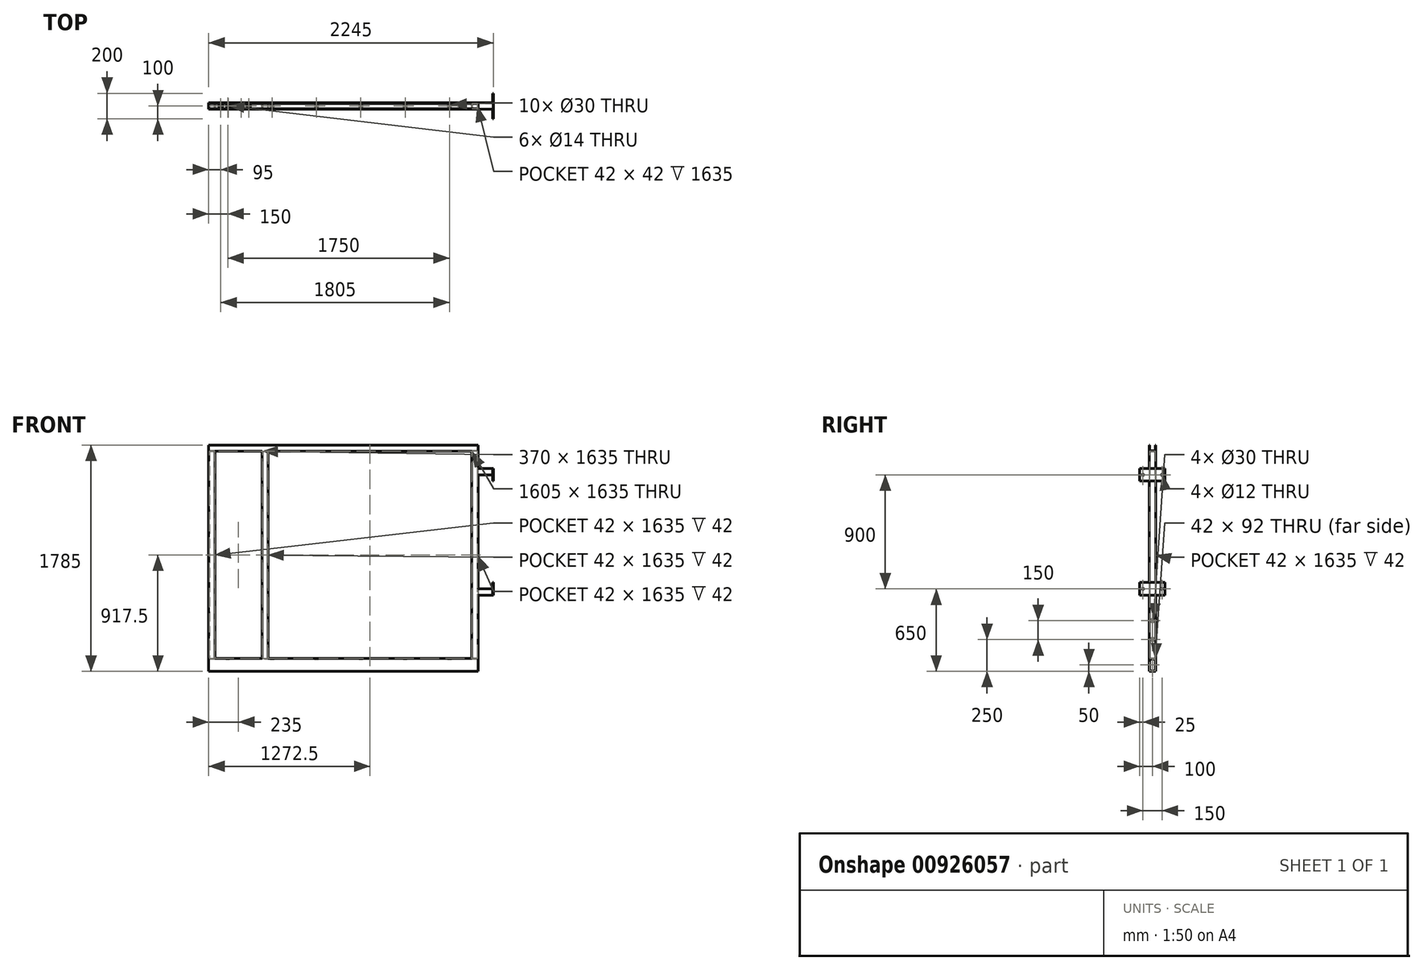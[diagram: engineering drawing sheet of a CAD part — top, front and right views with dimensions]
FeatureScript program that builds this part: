
annotation { "Feature Type Name" : "Feature", "Feature Type Description" : "" }
export const myFeature = defineFeature(function(context is Context, id is Id, definition is map)
    precondition{}
    {
        {
            var Q0;
            Q0=qCreatedBy(makeId("Top.planeOp"),FACE);
            var sketch = newSketch(context, id + "F0", { "sketchPlane" : qUnion([Q0])});
            skLineSegment(sketch, "E0.bottom", {"start": v(0, 0) * mm, "end": v(50, 0) * mm});
            skLineSegment(sketch, "E0.top", {"start": v(0, 50) * mm, "end": v(50, 50) * mm});
            skLineSegment(sketch, "E0.left", {"start": v(0, 0) * mm, "end": v(0, 4) * mm});
            skLineSegment(sketch, "E0.right", {"start": v(50, 0) * mm, "end": v(50, 50) * mm});
            skLineSegment(sketch, "E1.bottom", {"start": v(4, 46) * mm, "end": v(46, 46) * mm});
            skLineSegment(sketch, "E1.top", {"start": v(4, 4) * mm, "end": v(46, 4) * mm});
            skLineSegment(sketch, "E1.right", {"start": v(46, 46) * mm, "end": v(46, 4) * mm});
            skLineSegment(sketch, "E2", {"start": v(12.25, 50) * mm, "end": v(12.25, 46) * mm, "construction": true});
            skPoint(sketch, "E2.endSnap0", {"position": v(23, 46) * mm});
            skLineSegment(sketch, "E3", {"start": v(46, 38.8) * mm, "end": v(50, 38.8) * mm, "construction": true});
            skLineSegment(sketch, "E4", {"start": v(20.28, 4) * mm, "end": v(20.28, 0) * mm, "construction": true});
            skLineSegment(sketch, "E5.trimOffspring", {"start": v(0, 46) * mm, "end": v(0, 50) * mm});
            skLineSegment(sketch, "E6", {"start": v(0, 46) * mm, "end": v(0, 4) * mm});
            skLineSegment(sketch, "E7", {"start": v(4, 46) * mm, "end": v(4, 4) * mm});
            skSolve(sketch);
        }
        {
            var Q0;
            Q0 = qSketchRegion(id + "F0", true);
            extrude(context, id + "F1", {"entities" : qUnion([Q0]), "depth" : (1800 - 15 - 100 - 50) * mm, "offsetDistance" : 25 * mm});
        }
        {
            var Q0;
            Q0=makeQuery(id+"F1.opExtrude","SWEPT_FACE",FACE,{"disambiguationData":[OSD([sQuery(id+"F0.wireOp",EDGE,"E5.trimOffspring")])]});
            var sketch = newSketch(context, id + "F2", { "sketchPlane" : qUnion([Q0])});
            skLineSegment(sketch, "E8.bottom", {"start": v(-50, 0) * mm, "end": v(0, 0) * mm});
            skLineSegment(sketch, "E8.top", {"start": v(-50, -100) * mm, "end": v(0, -100) * mm});
            skLineSegment(sketch, "E8.left", {"start": v(-50, 0) * mm, "end": v(-50, -100) * mm});
            skLineSegment(sketch, "E8.right", {"start": v(0, 0) * mm, "end": v(0, -100) * mm});
            skLineSegment(sketch, "E9.bottom", {"start": v(-46, -4) * mm, "end": v(-4, -4) * mm});
            skLineSegment(sketch, "E9.top", {"start": v(-46, -96) * mm, "end": v(-4, -96) * mm});
            skLineSegment(sketch, "E9.left", {"start": v(-50, -4) * mm, "end": v(-50, -96) * mm});
            skLineSegment(sketch, "E9.right", {"start": v(-4, -4) * mm, "end": v(-4, -96) * mm});
            skLineSegment(sketch, "E10", {"start": v(-25, 0) * mm, "end": v(-25, -4) * mm, "construction": true});
            skLineSegment(sketch, "E11", {"start": v(-50, -50) * mm, "end": v(-50, -50) * mm});
            skLineSegment(sketch, "E12", {"start": v(-25, -100) * mm, "end": v(-25, -96) * mm, "construction": true});
            skLineSegment(sketch, "E13", {"start": v(-4, -50) * mm, "end": v(0, -50) * mm, "construction": true});
            skLineSegment(sketch, "E14", {"start": v(-46, -4) * mm, "end": v(-46, -96) * mm});
            skLineSegment(sketch, "E15", {"start": v(-46, -50) * mm, "end": v(-50, -50) * mm, "construction": true});
            skSolve(sketch);
        }
        {
            var Q0;
            Q0=makeQuery(id+"F2.imprint","IMPRINT",FACE,{"disambiguationData":[TD([[makeQuery(id+"F2.imprint","IMPRINT",EDGE,{"derivedFrom":sQuery(id+"F2.wireOp",EDGE,"E8.top")}),1.0]])]});
            extrude(context, id + "F3", {"entities" : qUnion([Q0]), "oppositeDirection" : true, "depth" : (100 + 1540 + 500 - 15) * mm, "offsetDistance" : 25 * mm});
        }
        {
            var Q0;
            Q0=qCreatedBy(makeId("Right.planeOp"),FACE);
            cPlane(context, id + "F4", {"entities" : qUnion([Q0]), "cplaneType" : CPlaneType.OFFSET, "offset" : (2125 / 2) * mm, "width" : 150 * mm, "height" : 150 * mm});
        }
        {
            var Q0;
            Q0=makeQuery(id+"F1.opExtrude","SWEPT_BODY",BODY,{"disambiguationData":[OSD([sQuery(id+"F0.wireOp",EDGE,"E0.bottom"),sQuery(id+"F0.wireOp",EDGE,"E0.top"),sQuery(id+"F0.wireOp",EDGE,"E0.left"),sQuery(id+"F0.wireOp",EDGE,"E0.right"),sQuery(id+"F0.wireOp",EDGE,"E1.bottom"),sQuery(id+"F0.wireOp",EDGE,"E1.top"),sQuery(id+"F0.wireOp",EDGE,"E1.right"),sQuery(id+"F0.wireOp",EDGE,"E5.trimOffspring")])]});
            var Q1;
            Q1=qCreatedBy(id+"F4.planeOp",FACE);
            mirror(context, id + "F5", {"operationType" : NewBodyOperationType.ADD, "entities" : qUnion([Q0]), "mirrorPlane" : qUnion([Q1])});
        }
        {
            var Q0;
            Q0=makeQuery(id+"F5.boolean.opBoolean","MERGE",FACE,{"derivedFrom":[makeQuery(id+"F1.opExtrude","SWEPT_FACE",FACE,{"disambiguationData":[OSD([sQuery(id+"F0.wireOp",EDGE,"E0.left")])]}),makeQuery(id+"F1.opExtrude","SWEPT_FACE",FACE,{"disambiguationData":[OSD([sQuery(id+"F0.wireOp",EDGE,"E5.trimOffspring")])]}),makeQuery(id+"F3.opExtrude","CAP_FACE",FACE,{"disambiguationData":[OSD([sQuery(id+"F2.wireOp",EDGE,"E8.bottom"),sQuery(id+"F2.wireOp",EDGE,"E8.top"),sQuery(id+"F2.wireOp",EDGE,"E8.left"),sQuery(id+"F2.wireOp",EDGE,"E8.right"),sQuery(id+"F2.wireOp",EDGE,"E9.bottom"),sQuery(id+"F2.wireOp",EDGE,"E9.top"),sQuery(id+"F2.wireOp",EDGE,"E9.left"),sQuery(id+"F2.wireOp",EDGE,"E9.right")])],"isStart":true})]});
            var sketch = newSketch(context, id + "F6", { "sketchPlane" : qUnion([Q0])});
            skLineSegment(sketch, "E16.bottom", {"start": v(-50, 1685) * mm, "end": v(-46, 1685) * mm});
            skLineSegment(sketch, "E16.top", {"start": v(-50, 1635) * mm, "end": v(0, 1635) * mm});
            skLineSegment(sketch, "E16.left", {"start": v(-50, 1685) * mm, "end": v(-50, 1635) * mm});
            skLineSegment(sketch, "E16.right", {"start": v(0, 1685) * mm, "end": v(0, 1635) * mm});
            skLineSegment(sketch, "E17.top", {"start": v(-46, 1639) * mm, "end": v(-4, 1639) * mm});
            skLineSegment(sketch, "E17.left", {"start": v(-46, 1685) * mm, "end": v(-46, 1639) * mm});
            skLineSegment(sketch, "E17.right", {"start": v(-4, 1685) * mm, "end": v(-4, 1639) * mm});
            skLineSegment(sketch, "E18", {"start": v(-25, 1639) * mm, "end": v(-25, 1635) * mm, "construction": true});
            skLineSegment(sketch, "E19.trimOffspring", {"start": v(-4, 1685) * mm, "end": v(0, 1685) * mm});
            skSolve(sketch);
        }
        {
            var Q0;
            Q0 = qSketchRegion(id + "F6", true);
            var Q1;
            Q1=makeQuery(id+"F5.boolean.opBoolean","MERGE",FACE,{"derivedFrom":[makeQuery(id+"F3.opExtrude","CAP_FACE",FACE,{"disambiguationData":[OSD([sQuery(id+"F2.wireOp",EDGE,"E8.bottom"),sQuery(id+"F2.wireOp",EDGE,"E8.top"),sQuery(id+"F2.wireOp",EDGE,"E8.left"),sQuery(id+"F2.wireOp",EDGE,"E8.right"),sQuery(id+"F2.wireOp",EDGE,"E9.bottom"),sQuery(id+"F2.wireOp",EDGE,"E9.top"),sQuery(id+"F2.wireOp",EDGE,"E9.left"),sQuery(id+"F2.wireOp",EDGE,"E9.right")])],"isStart":false}),makeQuery(id+"F5.opPattern","COPY",FACE,{"derivedFrom":makeQuery(id+"F1.opExtrude","SWEPT_FACE",FACE,{"disambiguationData":[OSD([sQuery(id+"F0.wireOp",EDGE,"E0.left")])]}),"instanceName":"1"}),makeQuery(id+"F5.opPattern","COPY",FACE,{"derivedFrom":makeQuery(id+"F1.opExtrude","SWEPT_FACE",FACE,{"disambiguationData":[OSD([sQuery(id+"F0.wireOp",EDGE,"E5.trimOffspring")])]}),"instanceName":"1"})]});
            extrude(context, id + "F7", {"entities" : qUnion([Q0]), "operationType" : NewBodyOperationType.ADD, "endBound" : BoundingType.UP_TO_SURFACE, "oppositeDirection" : true, "depth" : 25 * mm, "endBoundEntityFace" : qUnion([Q1]), "offsetDistance" : 25 * mm});
        }
        {
            var Q0;
            Q0=makeQuery(id+"F7.opExtrude","SWEPT_FACE",FACE,{"disambiguationData":[OSD([sQuery(id+"F6.wireOp",EDGE,"E17.top")])]});
            var sketch = newSketch(context, id + "F8", { "sketchPlane" : qUnion([Q0])});
            skLineSegment(sketch, "E20", {"start": v(2125, 25) * mm, "end": v(365, 25) * mm, "construction": true});
            skLineSegment(sketch, "E21", {"start": v(365, 4) * mm, "end": v(365, 46) * mm, "construction": true});
            skCircle(sketch, "E22", {"center": v(315, 25) * mm, "radius": 15 * mm});
            skCircle(sketch, "E23", {"center": v(155, 25) * mm, "radius": 15 * mm});
            skCircle(sketch, "E24", {"center": v(255, 25) * mm, "radius": 15 * mm});
            skCircle(sketch, "E25", {"center": v(95, 25) * mm, "radius": 15 * mm});
            skLineSegment(sketch, "E26", {"start": v(365, 25) * mm, "end": v(45, 25) * mm, "construction": true});
            skLineSegment(sketch, "E27", {"start": v(45, -20.75) * mm, "end": v(45, 62.6) * mm, "construction": true});
            skSolve(sketch);
        }
        {
            var Q0;
            Q0 = qSketchRegion(id + "F8", true);
            extrude(context, id + "F9", {"entities" : qUnion([Q0]), "operationType" : NewBodyOperationType.REMOVE, "oppositeDirection" : true, "depth" : 50 * mm, "offsetDistance" : 25 * mm});
        }
        {
            var Q0;
            Q0=makeQuery(id+"F1.opExtrude","SWEPT_FACE",FACE,{"disambiguationData":[OSD([sQuery(id+"F0.wireOp",EDGE,"E0.right")])]});
            var sketch = newSketch(context, id + "F10", { "sketchPlane" : qUnion([Q0])});
            skCircle(sketch, "E28", {"center": v(25, 300) * mm, "radius": 15 * mm});
            skLineSegment(sketch, "E29", {"start": v(25, 0) * mm, "end": v(25, 300) * mm, "construction": true});
            skCircle(sketch, "E30", {"center": v(25, 150) * mm, "radius": 15 * mm});
            skSolve(sketch);
        }
        {
            var Q0;
            Q0 = qSketchRegion(id + "F10", true);
            extrude(context, id + "F11", {"entities" : qUnion([Q0]), "operationType" : NewBodyOperationType.REMOVE, "oppositeDirection" : true, "depth" : 250 * mm, "offsetDistance" : 25 * mm});
        }
        {
            var Q0;
            Q0=makeQuery(id+"F7.boolean.opBoolean","MERGE",FACE,{"derivedFrom":[makeQuery(id+"F5.boolean.opBoolean","MERGE",FACE,{"derivedFrom":[makeQuery(id+"F3.opExtrude","CAP_FACE",FACE,{"disambiguationData":[OSD([sQuery(id+"F2.wireOp",EDGE,"E8.bottom"),sQuery(id+"F2.wireOp",EDGE,"E8.top"),sQuery(id+"F2.wireOp",EDGE,"E8.left"),sQuery(id+"F2.wireOp",EDGE,"E8.right"),sQuery(id+"F2.wireOp",EDGE,"E9.bottom"),sQuery(id+"F2.wireOp",EDGE,"E9.top"),sQuery(id+"F2.wireOp",EDGE,"E9.left"),sQuery(id+"F2.wireOp",EDGE,"E9.right")])],"isStart":false}),makeQuery(id+"F5.opPattern","COPY",FACE,{"derivedFrom":makeQuery(id+"F1.opExtrude","SWEPT_FACE",FACE,{"disambiguationData":[OSD([sQuery(id+"F0.wireOp",EDGE,"E0.left")])]}),"instanceName":"1"}),makeQuery(id+"F5.opPattern","COPY",FACE,{"derivedFrom":makeQuery(id+"F1.opExtrude","SWEPT_FACE",FACE,{"disambiguationData":[OSD([sQuery(id+"F0.wireOp",EDGE,"E5.trimOffspring")])]}),"instanceName":"1"})]}),makeQuery(id+"F7.opExtrude","CAP_FACE",FACE,{"disambiguationData":[OSD([sQuery(id+"F6.wireOp",EDGE,"E16.bottom"),sQuery(id+"F6.wireOp",EDGE,"E16.top"),sQuery(id+"F6.wireOp",EDGE,"E16.left"),sQuery(id+"F6.wireOp",EDGE,"E16.right"),sQuery(id+"F6.wireOp",EDGE,"E17.top"),sQuery(id+"F6.wireOp",EDGE,"E17.left"),sQuery(id+"F6.wireOp",EDGE,"E17.right"),sQuery(id+"F6.wireOp",EDGE,"E19.trimOffspring")])],"isStart":false})]});
            var sketch = newSketch(context, id + "F12", { "sketchPlane" : qUnion([Q0])});
            skLineSegment(sketch, "E31.bottom", {"start": v(0, 550) * mm, "end": v(4, 550) * mm});
            skLineSegment(sketch, "E31.top", {"start": v(0, 500) * mm, "end": v(50, 500) * mm});
            skLineSegment(sketch, "E31.left", {"start": v(0, 550) * mm, "end": v(0, 500) * mm});
            skLineSegment(sketch, "E31.right", {"start": v(50, 550) * mm, "end": v(50, 500) * mm});
            skLineSegment(sketch, "E32.top", {"start": v(4, 504) * mm, "end": v(46, 504) * mm});
            skLineSegment(sketch, "E32.left", {"start": v(4, 550) * mm, "end": v(4, 504) * mm});
            skLineSegment(sketch, "E32.right", {"start": v(46, 550) * mm, "end": v(46, 504) * mm});
            skLineSegment(sketch, "E33.trimOffspring", {"start": v(46, 550) * mm, "end": v(50, 550) * mm});
            skLineSegment(sketch, "E34", {"start": v(-400.98, 1000) * mm, "end": v(496.26, 1000) * mm, "construction": true});
            skLineSegment(sketch, "E35.MirrorCS", {"start": v(0, 1450) * mm, "end": v(4, 1450) * mm});
            skLineSegment(sketch, "E36.MirrorCS", {"start": v(46, 1450) * mm, "end": v(50, 1450) * mm});
            skLineSegment(sketch, "E37.MirrorCS", {"start": v(46, 1450) * mm, "end": v(46, 1496) * mm});
            skLineSegment(sketch, "E38.MirrorCS", {"start": v(50, 1450) * mm, "end": v(50, 1500) * mm});
            skLineSegment(sketch, "E39.MirrorCS", {"start": v(0, 1450) * mm, "end": v(0, 1500) * mm});
            skLineSegment(sketch, "E40.MirrorCS", {"start": v(4, 1496) * mm, "end": v(46, 1496) * mm});
            skLineSegment(sketch, "E41.MirrorCS", {"start": v(4, 1450) * mm, "end": v(4, 1496) * mm});
            skLineSegment(sketch, "E42.MirrorCS", {"start": v(0, 1500) * mm, "end": v(50, 1500) * mm});
            skSolve(sketch);
        }
        {
            var Q0;
            Q0 = qSketchRegion(id + "F12", true);
            extrude(context, id + "F13", {"entities" : qUnion([Q0]), "operationType" : NewBodyOperationType.ADD, "depth" : 116 * mm, "offsetDistance" : 25 * mm});
        }
        {
            var Q0;
            Q0=makeQuery(id+"F13.opExtrude","CAP_FACE",FACE,{"disambiguationData":[OSD([sQuery(id+"F12.wireOp",EDGE,"E35.MirrorCS"),sQuery(id+"F12.wireOp",EDGE,"E36.MirrorCS"),sQuery(id+"F12.wireOp",EDGE,"E37.MirrorCS"),sQuery(id+"F12.wireOp",EDGE,"E38.MirrorCS"),sQuery(id+"F12.wireOp",EDGE,"E39.MirrorCS"),sQuery(id+"F12.wireOp",EDGE,"E40.MirrorCS"),sQuery(id+"F12.wireOp",EDGE,"E41.MirrorCS"),sQuery(id+"F12.wireOp",EDGE,"E42.MirrorCS")])],"isStart":false});
            var sketch = newSketch(context, id + "F14", { "sketchPlane" : qUnion([Q0])});
            skLineSegment(sketch, "E43.bottom", {"start": v(125, 1500) * mm, "end": v(-75, 1500) * mm});
            skLineSegment(sketch, "E43.top", {"start": v(125, 1400) * mm, "end": v(-75, 1400) * mm});
            skLineSegment(sketch, "E43.left", {"start": v(125, 1500) * mm, "end": v(125, 1400) * mm});
            skLineSegment(sketch, "E43.right", {"start": v(-75, 1500) * mm, "end": v(-75, 1400) * mm});
            skPoint(sketch, "E44", {"position": v(25, 1500) * mm});
            skLineSegment(sketch, "E45.bottom", {"start": v(125, 600) * mm, "end": v(-75, 600) * mm});
            skLineSegment(sketch, "E45.top", {"start": v(125, 500) * mm, "end": v(-75, 500) * mm});
            skLineSegment(sketch, "E45.left", {"start": v(125, 600) * mm, "end": v(125, 500) * mm});
            skLineSegment(sketch, "E45.right", {"start": v(-75, 600) * mm, "end": v(-75, 500) * mm});
            skPoint(sketch, "E46", {"position": v(25, 500) * mm});
            skCircle(sketch, "E47", {"center": v(100, 1450) * mm, "radius": 6 * mm});
            skLineSegment(sketch, "E48", {"start": v(-50, 1450) * mm, "end": v(100, 1450) * mm, "construction": true});
            skLineSegment(sketch, "E49", {"start": v(25, 1400) * mm, "end": v(25, 1450) * mm, "construction": true});
            skLineSegment(sketch, "E50", {"start": v(-50, 550) * mm, "end": v(100, 550) * mm, "construction": true});
            skPoint(sketch, "E50.startSnap0", {"position": v(-75, 550) * mm});
            skLineSegment(sketch, "E51", {"start": v(25, 550) * mm, "end": v(25, 500) * mm, "construction": true});
            skCircle(sketch, "E52", {"center": v(-50, 550) * mm, "radius": 6 * mm});
            skCircle(sketch, "E53", {"center": v(100, 550) * mm, "radius": 6 * mm});
            skCircle(sketch, "E54", {"center": v(-50, 1450) * mm, "radius": 6 * mm});
            skSolve(sketch);
        }
        {
            var Q0;
            Q0 = qSketchRegion(id + "F14", true);
            extrude(context, id + "F15", {"entities" : qUnion([Q0]), "operationType" : NewBodyOperationType.ADD, "depth" : 4 * mm, "offsetDistance" : 25 * mm});
        }
        {
            var Q0;
            {var subQ2=makeQuery(id+"F1.opExtrude","SWEPT_FACE",FACE,{"disambiguationData":[OSD([sQuery(id+"F0.wireOp",EDGE,"E0.bottom")])]});Q0=makeQuery(id+"F5.boolean.opBoolean","SPLIT",FACE,{"disambiguationData":[TD([subQ2])],"derivedFrom":makeQuery(id+"F3.opExtrude","SWEPT_FACE",FACE,{"disambiguationData":[OSD([sQuery(id+"F2.wireOp",EDGE,"E8.bottom")])]})});}
            var sketch = newSketch(context, id + "F16", { "sketchPlane" : qUnion([Q0])});
            skLineSegment(sketch, "E55.bottom", {"start": v(470, 0) * mm, "end": v(420, 0) * mm});
            skLineSegment(sketch, "E55.top", {"start": v(470, 50) * mm, "end": v(420, 50) * mm});
            skLineSegment(sketch, "E55.left", {"start": v(470, 0) * mm, "end": v(470, 50) * mm});
            skLineSegment(sketch, "E55.right", {"start": v(420, 0) * mm, "end": v(420, 50) * mm});
            skLineSegment(sketch, "E56.bottom", {"start": v(424, 46) * mm, "end": v(466, 46) * mm});
            skLineSegment(sketch, "E56.top", {"start": v(424, 4) * mm, "end": v(466, 4) * mm});
            skLineSegment(sketch, "E56.left", {"start": v(424, 46) * mm, "end": v(424, 4) * mm});
            skLineSegment(sketch, "E56.right", {"start": v(466, 46) * mm, "end": v(466, 4) * mm});
            skSolve(sketch);
        }
        {
            var Q0;
            Q0 = qSketchRegion(id + "F16", true);
            var Q1;
            {var subQ2=makeQuery(id+"F1.opExtrude","SWEPT_FACE",FACE,{"disambiguationData":[OSD([sQuery(id+"F0.wireOp",EDGE,"E0.bottom")])]});Q1=makeQuery(id+"F7.boolean.opBoolean","SPLIT",FACE,{"disambiguationData":[TD([subQ2])],"derivedFrom":makeQuery(id+"F7.opExtrude","SWEPT_FACE",FACE,{"disambiguationData":[OSD([sQuery(id+"F6.wireOp",EDGE,"E16.top")])]})});}
            extrude(context, id + "F17", {"entities" : qUnion([Q0]), "operationType" : NewBodyOperationType.ADD, "endBound" : BoundingType.UP_TO_SURFACE, "depth" : 25 * mm, "endBoundEntityFace" : qUnion([Q1]), "offsetDistance" : 25 * mm});
        }
        {
            var Q0;
            Q0=makeQuery(id+"F3.opExtrude","SWEPT_FACE",FACE,{"disambiguationData":[OSD([sQuery(id+"F2.wireOp",EDGE,"E8.top")])]});
            var sketch = newSketch(context, id + "F18", { "sketchPlane" : qUnion([Q0])});
            skLineSegment(sketch, "E57", {"start": v(0, -25) * mm, "end": v(2125, -25) * mm, "construction": true});
            skCircle(sketch, "E58", {"center": v(150, -25) * mm, "radius": 7 * mm});
            skCircle(sketch, "E59.1.0.0", {"center": v(500, -25) * mm, "radius": 7 * mm});
            skCircle(sketch, "E59.2.0.0", {"center": v(850, -25) * mm, "radius": 7 * mm});
            skCircle(sketch, "E59.3.0.0", {"center": v(1200, -25) * mm, "radius": 7 * mm});
            skCircle(sketch, "E59.4.0.0", {"center": v(1550, -25) * mm, "radius": 7 * mm});
            skLineSegment(sketch, "E59.direction1", {"start": v(150, -25) * mm, "end": v(500, -25) * mm, "construction": true});
            skCircle(sketch, "E60.0.5.0", {"center": v(1900, -25) * mm, "radius": 7 * mm});
            skSolve(sketch);
        }
        {
            var Q0;
            Q0 = qSketchRegion(id + "F18", true);
            var Q1;
            Q1 = qConstructionFilter(qBodyType(qCreatedBy(id + "F18" ,EDGE), BodyType.WIRE), ConstructionObject.NO);
            extrude(context, id + "F19", {"entities" : qUnion([Q0]), "operationType" : NewBodyOperationType.REMOVE, "surfaceEntities" : qUnion([Q1]), "oppositeDirection" : true, "depth" : 125 * mm, "offsetDistance" : 25 * mm});
        }
        {
            var Q0;
            {var subQ2=makeQuery(id+"F1.opExtrude","SWEPT_FACE",FACE,{"disambiguationData":[OSD([sQuery(id+"F0.wireOp",EDGE,"E0.right")])]});var subQ3=makeQuery(id+"F5.opPattern","COPY",FACE,{"derivedFrom":subQ2,"instanceName":"1"});var subQ4=makeQuery(id+"F1.opExtrude","SWEPT_FACE",FACE,{"disambiguationData":[OSD([sQuery(id+"F0.wireOp",EDGE,"E0.bottom")])]});Q0=makeQuery(id+"F17.boolean.opBoolean","SPLIT",FACE,{"disambiguationData":[TD([subQ3])],"derivedFrom":makeQuery(id+"F5.boolean.opBoolean","SPLIT",FACE,{"disambiguationData":[TD([subQ4])],"derivedFrom":makeQuery(id+"F3.opExtrude","SWEPT_FACE",FACE,{"disambiguationData":[OSD([sQuery(id+"F2.wireOp",EDGE,"E8.bottom")])]})})});}
            var sketch = newSketch(context, id + "F20", { "sketchPlane" : qUnion([Q0])});
            skCircle(sketch, "E61", {"center": v(150, 25) * mm, "radius": 15 * mm});
            skCircle(sketch, "E62.1.0.0", {"center": v(500, 25) * mm, "radius": 15 * mm});
            skCircle(sketch, "E62.2.0.0", {"center": v(850, 25) * mm, "radius": 15 * mm});
            skCircle(sketch, "E62.3.0.0", {"center": v(1200, 25) * mm, "radius": 15 * mm});
            skCircle(sketch, "E62.4.0.0", {"center": v(1550, 25) * mm, "radius": 15 * mm});
            skCircle(sketch, "E62.5.0.0", {"center": v(1900, 25) * mm, "radius": 15 * mm});
            skLineSegment(sketch, "E62.direction1", {"start": v(150, 25) * mm, "end": v(500, 25) * mm, "construction": true});
            skSolve(sketch);
        }
        {
            var Q0;
            Q0=makeQuery(id+"F20.imprint","IMPRINT",FACE,{"disambiguationData":[TD([[makeQuery(id+"F20.imprint","IMPRINT",EDGE,{"derivedFrom":sQuery(id+"F20.wireOp",EDGE,"E62.1.0.0")}),1.0]])]});
            var Q1;
            Q1=makeQuery(id+"F20.imprint","IMPRINT",FACE,{"disambiguationData":[TD([[makeQuery(id+"F20.imprint","IMPRINT",EDGE,{"derivedFrom":sQuery(id+"F20.wireOp",EDGE,"E62.2.0.0")}),1.0]])]});
            var Q2;
            Q2=makeQuery(id+"F20.imprint","IMPRINT",FACE,{"disambiguationData":[TD([[makeQuery(id+"F20.imprint","IMPRINT",EDGE,{"derivedFrom":sQuery(id+"F20.wireOp",EDGE,"E62.3.0.0")}),1.0]])]});
            var Q3;
            Q3=makeQuery(id+"F20.imprint","IMPRINT",FACE,{"disambiguationData":[TD([[makeQuery(id+"F20.imprint","IMPRINT",EDGE,{"derivedFrom":sQuery(id+"F20.wireOp",EDGE,"E62.4.0.0")}),1.0]])]});
            var Q4;
            Q4=makeQuery(id+"F20.imprint","IMPRINT",FACE,{"disambiguationData":[TD([[makeQuery(id+"F20.imprint","IMPRINT",EDGE,{"derivedFrom":sQuery(id+"F20.wireOp",EDGE,"E62.5.0.0")}),1.0]])]});
            var Q5;
            Q5=makeQuery(id+"F20.imprint","IMPRINT",FACE,{"disambiguationData":[TD([[makeQuery(id+"F20.imprint","IMPRINT",EDGE,{"derivedFrom":sQuery(id+"F20.wireOp",EDGE,"E62.6.0.0")}),1.0]])]});
            var Q6;
            Q6=makeQuery(id+"F20.imprint","IMPRINT",FACE,{"disambiguationData":[TD([[makeQuery(id+"F20.imprint","IMPRINT",EDGE,{"derivedFrom":sQuery(id+"F20.wireOp",EDGE,"E61")}),1.0]])]});
            var Q7;
            Q7 = qConstructionFilter(qBodyType(qCreatedBy(id + "F20" ,EDGE), BodyType.WIRE), ConstructionObject.NO);
            extrude(context, id + "F21", {"entities" : qUnion([Q0, Q1, Q2, Q3, Q4, Q5, Q6]), "operationType" : NewBodyOperationType.REMOVE, "surfaceEntities" : qUnion([Q7]), "oppositeDirection" : true, "depth" : 5 * mm, "offsetDistance" : 25 * mm});
        }
    });
